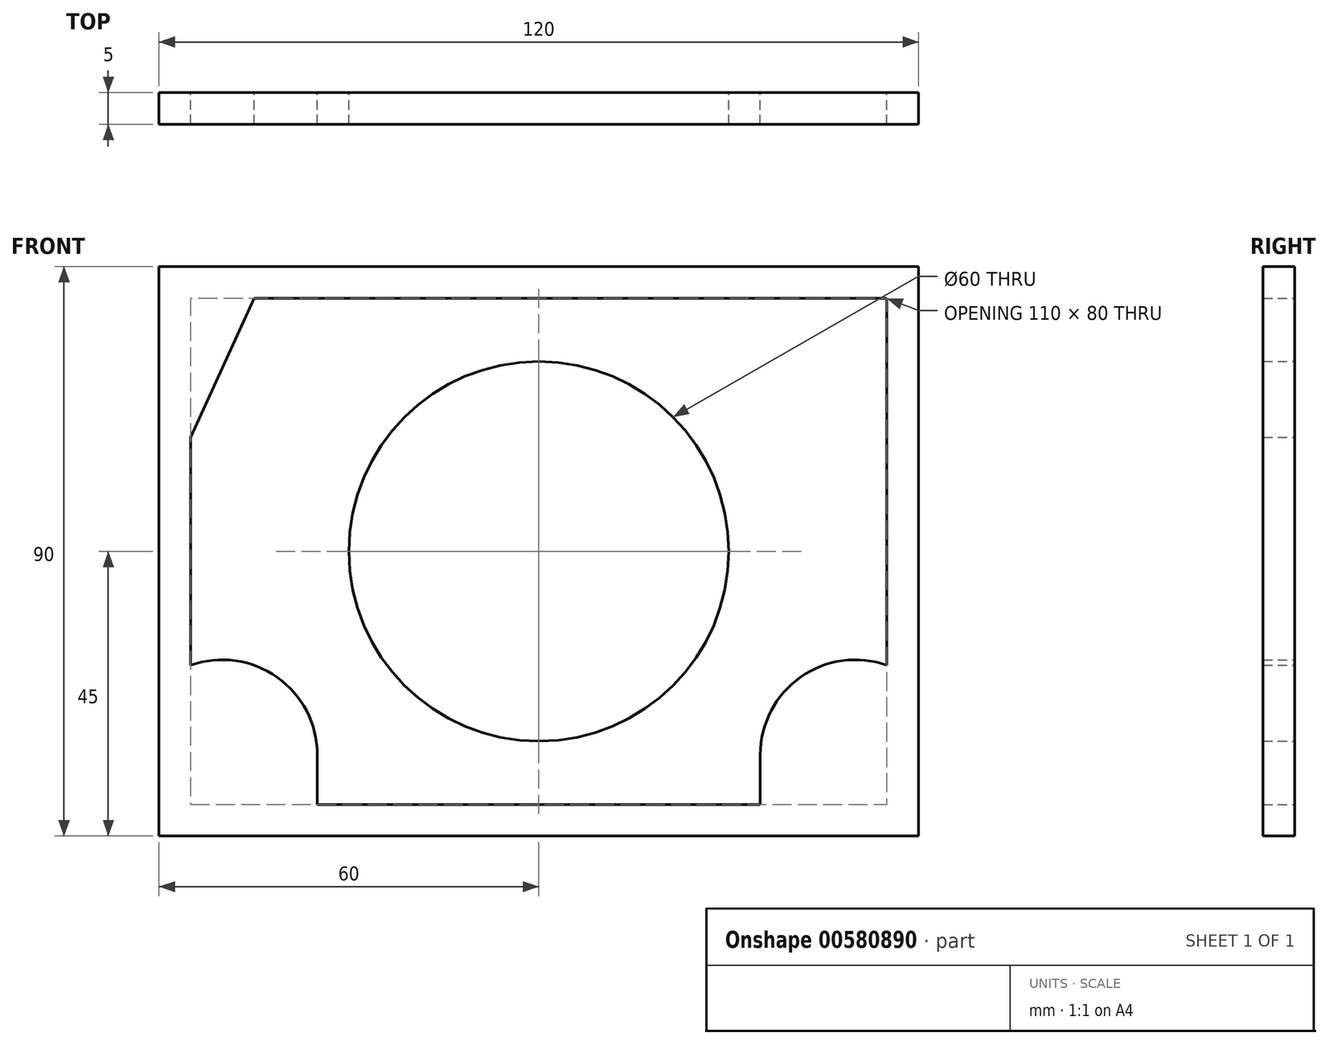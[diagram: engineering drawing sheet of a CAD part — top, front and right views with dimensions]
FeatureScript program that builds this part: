
annotation { "Feature Type Name" : "Feature", "Feature Type Description" : "" }
export const myFeature = defineFeature(function(context is Context, id is Id, definition is map)
    precondition{}
    {
        {
            var Q0;
            Q0=qCreatedBy(makeId("Front.planeOp"),FACE);
            var sketch = newSketch(context, id + "F0", { "sketchPlane" : qUnion([Q0])});
            skLineSegment(sketch, "E0", {"start": v(-30, 0) * mm, "end": v(36.74, 0) * mm, "construction": true});
            skLineSegment(sketch, "E1", {"start": v(-55, 18) * mm, "end": v(-55, -18) * mm});
            skLineSegment(sketch, "E2", {"start": v(-55, 18) * mm, "end": v(-45, 40) * mm});
            skLineSegment(sketch, "E3", {"start": v(-45, 40) * mm, "end": v(55, 40) * mm});
            skLineSegment(sketch, "E4", {"start": v(55, 40) * mm, "end": v(55, 0) * mm});
            skLineSegment(sketch, "E5", {"start": v(55, 0) * mm, "end": v(55, -18) * mm});
            skLineSegment(sketch, "E6", {"start": v(-35, -40) * mm, "end": v(35, -40) * mm});
            skLineSegment(sketch, "E7", {"start": v(-60, 45) * mm, "end": v(-60, -45) * mm});
            skLineSegment(sketch, "E8", {"start": v(-60, -45) * mm, "end": v(60, -45) * mm});
            skLineSegment(sketch, "E9", {"start": v(-60, 45) * mm, "end": v(60, 45) * mm});
            skLineSegment(sketch, "E10", {"start": v(60, 45) * mm, "end": v(60, -45) * mm});
            skLineSegment(sketch, "E11", {"start": v(-35, -40) * mm, "end": v(-35, -32.14) * mm});
            skLineSegment(sketch, "E12", {"start": v(35, -40) * mm, "end": v(35, -32.14) * mm});
            skArc(sketch, "E13", {"start": v(-35, -32.14) * mm, "mid": v(-41.34, -19.9) * mm, "end": v(-55, -18) * mm});
            skArc(sketch, "E14", {"start": v(55, -18) * mm, "mid": v(41.34, -19.9) * mm, "end": v(35, -32.14) * mm});
            skLineSegment(sketch, "E15", {"start": v(0, 36.7) * mm, "end": v(0, -31.8) * mm, "construction": true});
            skArc(sketch, "E16", {"start": v(-30, 0) * mm, "mid": v(0, 30) * mm, "end": v(30, 0) * mm});
            skArc(sketch, "E17.MirrorCS", {"start": v(-30, 0) * mm, "mid": v(0, -30) * mm, "end": v(30, 0) * mm});
            skArc(sketch, "E18", {"start": v(-20, 0) * mm, "mid": v(0, 20) * mm, "end": v(20, 0) * mm, "construction": true});
            skArc(sketch, "E19.MirrorCS", {"start": v(-20, 0) * mm, "mid": v(0, -20) * mm, "end": v(20, 0) * mm, "construction": true});
            skCircle(sketch, "E20", {"center": v(-20, 0) * mm, "radius": 3 * mm});
            skCircle(sketch, "E21", {"center": v(0, 20) * mm, "radius": 3 * mm});
            skCircle(sketch, "E22", {"center": v(-15.2, 13) * mm, "radius": 3 * mm});
            skCircle(sketch, "E23.MirrorC", {"center": v(0, -20) * mm, "radius": 3 * mm});
            skCircle(sketch, "E24.MirrorC", {"center": v(-15.2, -13) * mm, "radius": 3 * mm});
            skLineSegment(sketch, "E25.MirrorCS", {"start": v(0, -36.7) * mm, "end": v(0, 31.8) * mm, "construction": true});
            skCircle(sketch, "E26.MirrorC", {"center": v(15.2, 13) * mm, "radius": 3 * mm});
            skCircle(sketch, "E27.MirrorC", {"center": v(20, 0) * mm, "radius": 3 * mm});
            skCircle(sketch, "E28.MirrorC", {"center": v(15.2, -13) * mm, "radius": 3 * mm});
            skSolve(sketch);
        }
        {
            var Q0;
            Q0=makeQuery(id+"F0.imprint","IMPRINT",FACE,{"disambiguationData":[TD([[makeQuery(id+"F0.imprint","IMPRINT",EDGE,{"derivedFrom":sQuery(id+"F0.wireOp",EDGE,"E1")}),-1.0]])]});
            extrude(context, id + "F1", {"entities" : qUnion([Q0]), "depth" : 5 * mm, "offsetDistance" : 25 * mm});
        }
        {
            var Q0;
            Q0=makeQuery(id+"F0.imprint","IMPRINT",FACE,{"disambiguationData":[TD([[makeQuery(id+"F0.imprint","IMPRINT",EDGE,{"derivedFrom":sQuery(id+"F0.wireOp",EDGE,"E1")}),1.0]])]});
            extrude(context, id + "F2", {"entities" : qUnion([Q0]), "operationType" : NewBodyOperationType.ADD, "oppositeDirection" : true, "depth" : 5 * mm, "offsetDistance" : 25 * mm});
        }
        {
            var Q0;
            Q0=makeQuery(id+"F0.imprint","IMPRINT",FACE,{"disambiguationData":[TD([[makeQuery(id+"F0.imprint","IMPRINT",EDGE,{"derivedFrom":sQuery(id+"F0.wireOp",EDGE,"E22")}),1.0]])]});
            var Q1;
            Q1=makeQuery(id+"F0.imprint","IMPRINT",FACE,{"disambiguationData":[TD([[makeQuery(id+"F0.imprint","IMPRINT",EDGE,{"derivedFrom":sQuery(id+"F0.wireOp",EDGE,"E21")}),-1.0]])]});
            var Q2;
            Q2=makeQuery(id+"F0.imprint","IMPRINT",FACE,{"disambiguationData":[TD([[makeQuery(id+"F0.imprint","IMPRINT",EDGE,{"derivedFrom":sQuery(id+"F0.wireOp",EDGE,"E26.MirrorC")}),-1.0]])]});
            var Q3;
            Q3=makeQuery(id+"F0.imprint","IMPRINT",FACE,{"disambiguationData":[TD([[makeQuery(id+"F0.imprint","IMPRINT",EDGE,{"derivedFrom":sQuery(id+"F0.wireOp",EDGE,"E27.MirrorC")}),-1.0]])]});
            var Q4;
            Q4=makeQuery(id+"F0.imprint","IMPRINT",FACE,{"disambiguationData":[TD([[makeQuery(id+"F0.imprint","IMPRINT",EDGE,{"derivedFrom":sQuery(id+"F0.wireOp",EDGE,"E28.MirrorC")}),1.0]])]});
            var Q5;
            Q5=makeQuery(id+"F0.imprint","IMPRINT",FACE,{"disambiguationData":[TD([[makeQuery(id+"F0.imprint","IMPRINT",EDGE,{"derivedFrom":sQuery(id+"F0.wireOp",EDGE,"E23.MirrorC")}),-1.0]])]});
            var Q6;
            Q6=makeQuery(id+"F0.imprint","IMPRINT",FACE,{"disambiguationData":[TD([[makeQuery(id+"F0.imprint","IMPRINT",EDGE,{"derivedFrom":sQuery(id+"F0.wireOp",EDGE,"E24.MirrorC")}),-1.0]])]});
            var Q7;
            Q7=makeQuery(id+"F0.imprint","IMPRINT",FACE,{"disambiguationData":[TD([[makeQuery(id+"F0.imprint","IMPRINT",EDGE,{"derivedFrom":sQuery(id+"F0.wireOp",EDGE,"E20")}),-1.0]])]});
            extrude(context, id + "F3", {"entities" : qUnion([Q0, Q1, Q2, Q3, Q4, Q5, Q6, Q7]), "operationType" : NewBodyOperationType.REMOVE, "depth" : 25 * mm, "offsetDistance" : 25 * mm});
        }
        {
            var Q0;
            Q0=makeQuery(id+"F0.imprint","IMPRINT",FACE,{"disambiguationData":[TD([[makeQuery(id+"F0.imprint","IMPRINT",EDGE,{"derivedFrom":sQuery(id+"F0.wireOp",EDGE,"E16")}),-1.0]])]});
            extrude(context, id + "F4", {"entities" : qUnion([Q0]), "operationType" : NewBodyOperationType.REMOVE, "oppositeDirection" : true, "depth" : 5 * mm, "offsetDistance" : 25 * mm});
        }
        {
            var Q0;
            Q0=makeQuery(id+"F0.imprint","IMPRINT",FACE,{"disambiguationData":[TD([[makeQuery(id+"F0.imprint","IMPRINT",EDGE,{"derivedFrom":sQuery(id+"F0.wireOp",EDGE,"E16")}),-1.0]])]});
            extrude(context, id + "F5", {"entities" : qUnion([Q0]), "depth" : 5 * mm, "offsetDistance" : 25 * mm});
        }
    });
